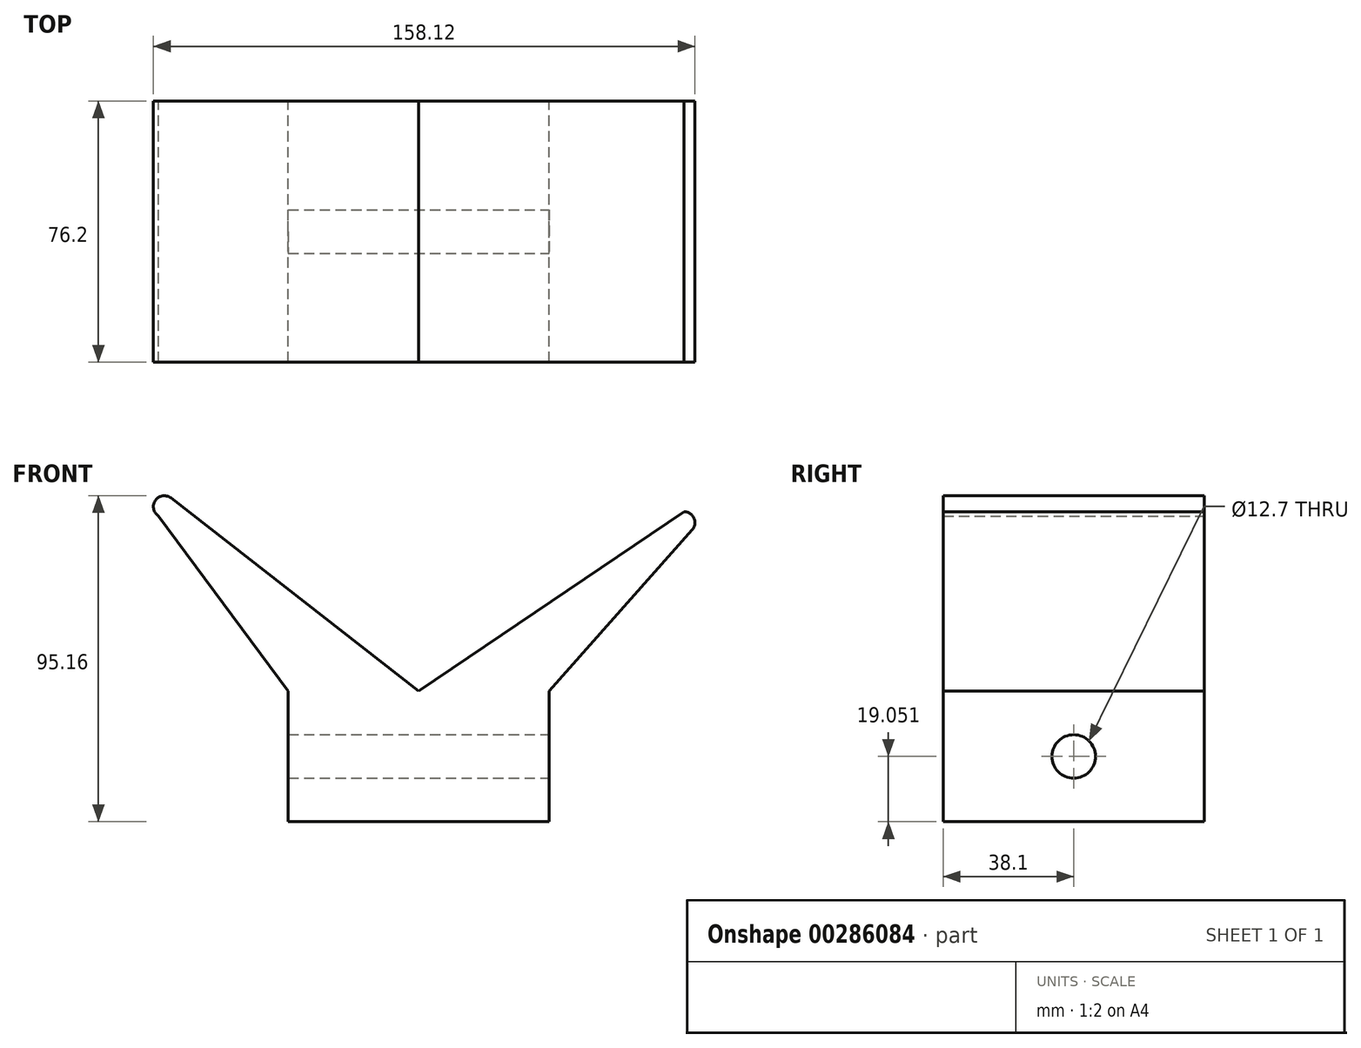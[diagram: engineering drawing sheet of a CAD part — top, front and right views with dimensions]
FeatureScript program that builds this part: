
annotation { "Feature Type Name" : "Feature", "Feature Type Description" : "" }
export const myFeature = defineFeature(function(context is Context, id is Id, definition is map)
    precondition{}
    {
        {
            var Q0;
            Q0=qCreatedBy(makeId("Front.planeOp"),FACE);
            var sketch = newSketch(context, id + "F0", { "sketchPlane" : qUnion([Q0])});
            skLineSegment(sketch, "E0", {"start": v(-76, -65.06) * mm, "end": v(0.2, -65.06) * mm});
            skLineSegment(sketch, "E1", {"start": v(-76, -65.06) * mm, "end": v(-76, -26.96) * mm});
            skLineSegment(sketch, "E2", {"start": v(0.2, -65.06) * mm, "end": v(0.2, -26.96) * mm});
            skCircle(sketch, "E3", {"center": v(-112.2, 26.92) * mm, "radius": 3.18 * mm});
            skCircle(sketch, "E4", {"center": v(39.58, 22.25) * mm, "radius": 3.18 * mm});
            skLineSegment(sketch, "E5", {"start": v(-113.83, 24.2) * mm, "end": v(-76, -26.96) * mm});
            skLineSegment(sketch, "E6", {"start": v(0.2, -26.96) * mm, "end": v(41.95, 20.15) * mm});
            skLineSegment(sketch, "E7", {"start": v(-37.9, -26.96) * mm, "end": v(-110.24, 29.43) * mm});
            skLineSegment(sketch, "E8", {"start": v(-37.9, -26.96) * mm, "end": v(39.58, 25.43) * mm});
            skSolve(sketch);
        }
        {
            var Q0;
            Q0=makeQuery(id+"F0.imprint","IMPRINT",FACE,{"disambiguationData":[TD([[makeQuery(id+"F0.imprint","IMPRINT",EDGE,{"derivedFrom":sQuery(id+"F0.wireOp",EDGE,"E0")}),1.0]])]});
            var Q1;
            {var subQ0=sQuery(id+"F0.wireOp",EDGE,"E4");var subQ1=makeQuery(id+"F0.imprint","INTERSECT",VERTEX,{"derivedFrom":[subQ0,sQuery(id+"F0.wireOp",EDGE,"E6")]});Q1=makeQuery(id+"F0.imprint","IMPRINT",FACE,{"disambiguationData":[TD([[makeQuery(id+"F0.imprint","IMPRINT",EDGE,{"disambiguationData":[TD([[subQ1,1.0]])],"derivedFrom":subQ0}),1.0]])]});}
            var Q2;
            {var subQ0=sQuery(id+"F0.wireOp",EDGE,"E3");var subQ1=makeQuery(id+"F0.imprint","INTERSECT",VERTEX,{"derivedFrom":[subQ0,sQuery(id+"F0.wireOp",EDGE,"E5")]});Q2=makeQuery(id+"F0.imprint","IMPRINT",FACE,{"disambiguationData":[TD([[makeQuery(id+"F0.imprint","IMPRINT",EDGE,{"disambiguationData":[TD([[subQ1,1.0]])],"derivedFrom":subQ0}),1.0]])]});}
            extrude(context, id + "F1", {"entities" : qUnion([Q0, Q1, Q2]), "depth" : 76.2 * mm});
        }
        {
            var Q0;
            Q0=makeQuery(id+"F1.opExtrude","CAP_FACE",FACE,{"disambiguationData":[OSD([sQuery(id+"F0.wireOp",EDGE,"E0"),sQuery(id+"F0.wireOp",EDGE,"E1"),sQuery(id+"F0.wireOp",EDGE,"E2"),sQuery(id+"F0.wireOp",EDGE,"E3"),sQuery(id+"F0.wireOp",EDGE,"E4"),sQuery(id+"F0.wireOp",EDGE,"E5"),sQuery(id+"F0.wireOp",EDGE,"E6"),sQuery(id+"F0.wireOp",EDGE,"E7"),sQuery(id+"F0.wireOp",EDGE,"E8")])],"isStart":true});
            extrude(context, id + "F2", {"entities" : qUnion([Q0]), "operationType" : NewBodyOperationType.REMOVE, "depth" : 211.58 * mm});
        }
        {
            var Q0;
            Q0=makeQuery(id+"F1.opExtrude","SWEPT_FACE",FACE,{"disambiguationData":[OSD([sQuery(id+"F0.wireOp",EDGE,"E2")])]});
            var sketch = newSketch(context, id + "F3", { "sketchPlane" : qUnion([Q0])});
            skCircle(sketch, "E9", {"center": v(-38.1, -46) * mm, "radius": 6.35 * mm});
            skSolve(sketch);
        }
        {
            var Q0;
            Q0 = qSketchRegion(id + "F3", true);
            extrude(context, id + "F4", {"entities" : qUnion([Q0]), "operationType" : NewBodyOperationType.REMOVE, "oppositeDirection" : true, "depth" : 296.93 * mm});
        }
    });
